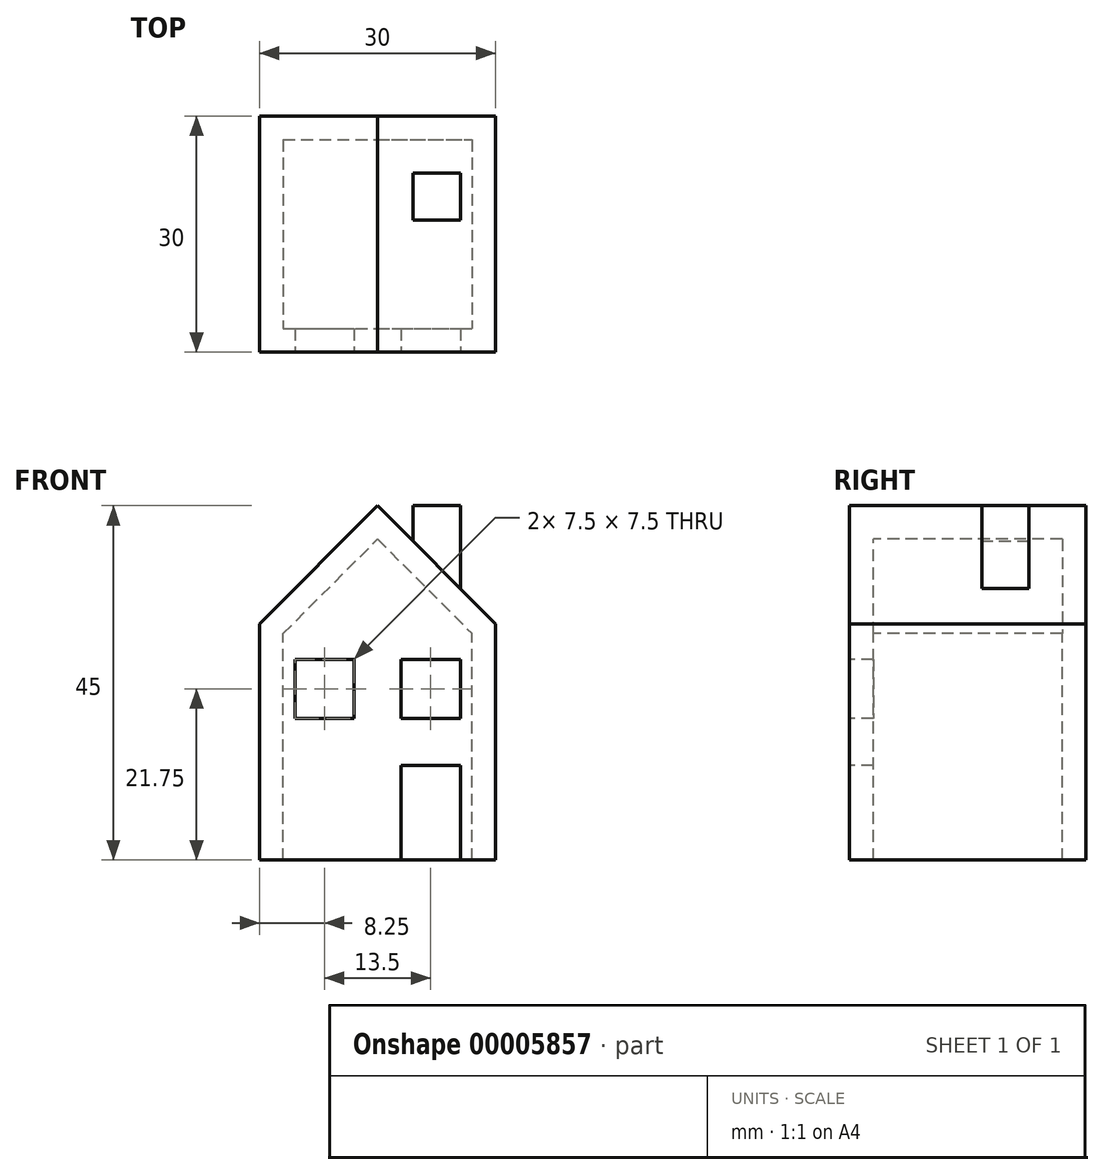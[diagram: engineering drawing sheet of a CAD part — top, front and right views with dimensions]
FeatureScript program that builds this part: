
annotation { "Feature Type Name" : "Feature", "Feature Type Description" : "" }
export const myFeature = defineFeature(function(context is Context, id is Id, definition is map)
    precondition{}
    {
        {
            var Q0;
            Q0=qCreatedBy(makeId("Front.planeOp"),FACE);
            var sketch = newSketch(context, id + "F0", { "sketchPlane" : qUnion([Q0])});
            skLineSegment(sketch, "E0.bottom", {"start": v(0, 0) * mm, "end": v(20, 0) * mm});
            skLineSegment(sketch, "E0.top", {"start": v(0, 20) * mm, "end": v(20, 20) * mm});
            skLineSegment(sketch, "E0.left", {"start": v(0, 0) * mm, "end": v(0, 20) * mm});
            skLineSegment(sketch, "E0.right", {"start": v(20, 0) * mm, "end": v(20, 20) * mm});
            skLineSegment(sketch, "E1", {"start": v(0, 20) * mm, "end": v(10, 30) * mm});
            skLineSegment(sketch, "E2", {"start": v(10, 30) * mm, "end": v(20, 20) * mm});
            skSolve(sketch);
        }
        {
            var Q0;
            Q0=makeQuery(id+"F0.imprint","IMPRINT",FACE,{"disambiguationData":[TD([[makeQuery(id+"F0.imprint","IMPRINT",EDGE,{"derivedFrom":sQuery(id+"F0.wireOp",EDGE,"E0.bottom")}),1.0]])]});
            var Q1;
            Q1=makeQuery(id+"F0.imprint","IMPRINT",FACE,{"disambiguationData":[TD([[makeQuery(id+"F0.imprint","IMPRINT",EDGE,{"derivedFrom":sQuery(id+"F0.wireOp",EDGE,"E0.top")}),1.0]])]});
            extrude(context, id + "F1", {"entities" : qUnion([Q0, Q1]), "oppositeDirection" : true, "depth" : 20 * mm});
        }
        {
            var Q0;
            Q0=makeQuery(id+"F1.opExtrude","SWEPT_FACE",FACE,{"disambiguationData":[OSD([sQuery(id+"F0.wireOp",EDGE,"E0.bottom")])]});
            shell(context, id + "F2", {"entities" : qUnion([Q0]), "thickness" : 2 * mm});
        }
        {
            var Q0;
            Q0=makeQuery(id+"F1.opExtrude","CAP_FACE",FACE,{"disambiguationData":[OSD([sQuery(id+"F0.wireOp",EDGE,"E0.bottom"),sQuery(id+"F0.wireOp",EDGE,"E0.left"),sQuery(id+"F0.wireOp",EDGE,"E0.right"),sQuery(id+"F0.wireOp",EDGE,"E1"),sQuery(id+"F0.wireOp",EDGE,"E2")])],"isStart":true});
            var sketch = newSketch(context, id + "F3", { "sketchPlane" : qUnion([Q0])});
            skLineSegment(sketch, "E3.bottom", {"start": v(12, 0) * mm, "end": v(17, 0) * mm});
            skLineSegment(sketch, "E3.top", {"start": v(12, 8) * mm, "end": v(17, 8) * mm});
            skLineSegment(sketch, "E3.left", {"start": v(12, 0) * mm, "end": v(12, 8) * mm});
            skLineSegment(sketch, "E3.right", {"start": v(17, 0) * mm, "end": v(17, 8) * mm});
            skLineSegment(sketch, "E4.bottom", {"start": v(3, 17) * mm, "end": v(8, 17) * mm});
            skLineSegment(sketch, "E4.top", {"start": v(3, 12) * mm, "end": v(8, 12) * mm});
            skLineSegment(sketch, "E4.left", {"start": v(3, 17) * mm, "end": v(3, 12) * mm});
            skLineSegment(sketch, "E4.right", {"start": v(8, 17) * mm, "end": v(8, 12) * mm});
            skLineSegment(sketch, "E5.bottom", {"start": v(12, 17) * mm, "end": v(17, 17) * mm});
            skLineSegment(sketch, "E5.top", {"start": v(12, 12) * mm, "end": v(17, 12) * mm});
            skLineSegment(sketch, "E5.left", {"start": v(12, 17) * mm, "end": v(12, 12) * mm});
            skLineSegment(sketch, "E5.right", {"start": v(17, 17) * mm, "end": v(17, 12) * mm});
            skSolve(sketch);
        }
        {
            var Q0;
            Q0=makeQuery(id+"F3.imprint","IMPRINT",FACE,{"disambiguationData":[TD([[makeQuery(id+"F3.imprint","IMPRINT",EDGE,{"derivedFrom":sQuery(id+"F3.wireOp",EDGE,"E4.bottom")}),-1.0]])]});
            var Q1;
            Q1=makeQuery(id+"F3.imprint","IMPRINT",FACE,{"disambiguationData":[TD([[makeQuery(id+"F3.imprint","IMPRINT",EDGE,{"derivedFrom":sQuery(id+"F3.wireOp",EDGE,"E5.bottom")}),-1.0]])]});
            var Q2;
            Q2=makeQuery(id+"F3.imprint","IMPRINT",FACE,{"disambiguationData":[TD([[makeQuery(id+"F3.imprint","IMPRINT",EDGE,{"derivedFrom":sQuery(id+"F3.wireOp",EDGE,"E3.bottom")}),1.0]])]});
            var Q3;
            {var subQ0=sQuery(id+"F0.wireOp",EDGE,"E0.bottom");var subQ1=sQuery(id+"F0.wireOp",EDGE,"E0.left");var subQ2=sQuery(id+"F0.wireOp",EDGE,"E0.right");var subQ3=sQuery(id+"F0.wireOp",EDGE,"E1");var subQ4=sQuery(id+"F0.wireOp",EDGE,"E2");Q3=makeQuery(id+"F2.opShell","OFFSET_FACE",FACE,{"disambiguationData":[OSD([subQ0,subQ1,subQ2,subQ3,subQ4]),TDD([makeQuery(id+"F1.opExtrude","CAP_FACE",FACE,{"disambiguationData":[OSD([subQ0,subQ1,subQ2,subQ3,subQ4])],"isStart":false})])]});}
            extrude(context, id + "F4", {"entities" : qUnion([Q0, Q1, Q2]), "operationType" : NewBodyOperationType.REMOVE, "endBound" : BoundingType.UP_TO_SURFACE, "oppositeDirection" : true, "endBoundEntityFace" : qUnion([Q3]), "depth" : 25 * mm});
        }
        {
            var Q0;
            Q0=makeQuery(id+"F1.opExtrude","SWEPT_FACE",FACE,{"disambiguationData":[OSD([sQuery(id+"F0.wireOp",EDGE,"E0.bottom")])]});
            cPlane(context, id + "F5", {"entities" : qUnion([Q0]), "cplaneType" : CPlaneType.OFFSET, "offset" : 30 * mm, "oppositeDirection" : true, "width" : 150 * mm, "height" : 150 * mm});
        }
        {
            var Q0;
            Q0=qCreatedBy(id+"F5.planeOp",FACE);
            var sketch = newSketch(context, id + "F6", { "sketchPlane" : qUnion([Q0])});
            skLineSegment(sketch, "E6.bottom", {"start": v(13.02, -15.19) * mm, "end": v(17.02, -15.19) * mm});
            skLineSegment(sketch, "E6.top", {"start": v(13.02, -11.19) * mm, "end": v(17.02, -11.19) * mm});
            skLineSegment(sketch, "E6.left", {"start": v(13.02, -15.19) * mm, "end": v(13.02, -11.19) * mm});
            skLineSegment(sketch, "E6.right", {"start": v(17.02, -15.19) * mm, "end": v(17.02, -11.19) * mm});
            skSolve(sketch);
        }
        {
            var Q0;
            Q0=makeQuery(id+"F6.imprint","IMPRINT",FACE,{"disambiguationData":[TD([[makeQuery(id+"F6.imprint","IMPRINT",EDGE,{"derivedFrom":sQuery(id+"F6.wireOp",EDGE,"E6.bottom")}),1.0]])]});
            var Q1;
            Q1=makeQuery(id+"F1.opExtrude","SWEPT_FACE",FACE,{"disambiguationData":[OSD([sQuery(id+"F0.wireOp",EDGE,"E2")])]});
            extrude(context, id + "F7", {"entities" : qUnion([Q0]), "operationType" : NewBodyOperationType.ADD, "endBound" : BoundingType.UP_TO_SURFACE, "endBoundEntityFace" : qUnion([Q1]), "depth" : 25 * mm});
        }
        {
            var Q0;
            Q0=makeQuery(id+"F1.opExtrude","SWEPT_BODY",BODY,{"disambiguationData":[OSD([sQuery(id+"F0.wireOp",EDGE,"E0.bottom"),sQuery(id+"F0.wireOp",EDGE,"E0.left"),sQuery(id+"F0.wireOp",EDGE,"E0.right"),sQuery(id+"F0.wireOp",EDGE,"E1"),sQuery(id+"F0.wireOp",EDGE,"E2")])]});
            var Q1;
            Q1=qCreatedBy(makeId("Origin.pointOp"),VERTEX);
            transform(context, id + "F8", {"entities" : qUnion([Q0]), "transformType" : TransformType.SCALE_UNIFORMLY, "scale" : 1.5, "makeCopy" : false, "scalePoint" : qUnion([Q1])});
        }
    });
